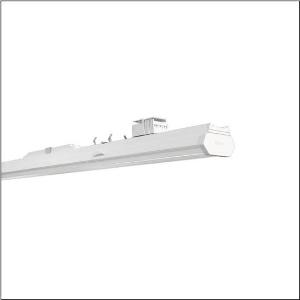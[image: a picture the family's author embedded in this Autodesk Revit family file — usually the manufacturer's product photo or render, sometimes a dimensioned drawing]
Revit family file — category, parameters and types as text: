
# Revit family: licross_r__11_protected_ho_51td11cn4exs_ee6c
name_source: partatom
category: Lighting Fixtures
units: mm (PartAtom-declared; Revit-internal decimal feet)

## family parameters
Cut with Voids When Loaded = No
Host = Face
Light Source = No
Part Type = Normal
Room Calculation Point = No
Round Connector Dimension = Use Diameter
Shared = No

## types (1)
- --- (1 x LED, 14460 lm, 77.6 W, 4000K)
    Apparent Load = 78 VA
    CIE Flux Codes = 84 94 98 99 100
    Color Rendering = 80
    Color Temperature = 4000K
    Default Elevation = 1800 mm
    Description = Licross® 11 Protected HO, luminaire insert, of sheet steel, galvanised, coil coated, white, length: 1.500mm, width: 90mm, height: 101mm, LED rated luminous flux: 14.460lm, light colour: 840, control gear: ON/OFF Multilumen, CLOi, with plug, 3-pole, with phase selection, mains connection: 220..240V, AC, 50/60Hz, start of lifetime: 78W, end of service life: 87W, halogen-free wiring, primary light control with lens, of plastic, primary optical cover: cover, of PMMA, light emission: direct distribution, primary light characteristic: symmetric, protection rating (complete): IP54, insulation class (complete): insulation class I (protective earthing), certification: CE, ENEC, VDE, UKCA, protection symbol: D if used in an environment with non-conductive dust loads with corresponding accessories, impact resistance: IK06, permissible ambient temperature for indoor applications: -35..+35°C, corresponds to IFS (International Featured Standards) requirements for safety and quality in the food industry, reducing of maximum allowable ambient temperature of 5°C with ceiling mounting, LABS conformity tested according to VDMA 24364:2018-05, packaging unit: 1 piece
    Height = 92 mm
    Lamp = 1 x LED
    Lamp Light Flux = 14460 lm
    Lamp Power = 77.6 W
    Lamp count = 1
    Length = 1500 mm
    Luminous efficacy = 186 lm/W
    Manufacturer = Siteco
    ModVariant = No
    Model = 51TD11CN4EXS
    Mounting Place = Ceiling
    Mounting Type = Pendant
    Number of Poles = 1
    OnlyDefault = Yes
    Power Factor = 1
    Product Name = Licross® 11 Protected HO
    Product group = luminaire insert
    ProductGroupID = 901
    Protection Class = Protection class I
    Protection Degree = IP 54
    RLX_Detail_Level = 1
    RLX_Emergency_Light_Flux = 0 lm
    RLX_Emergency_Type = 0
    RLX_Emergency_Type_DB = No
    RlxData = <blob elided: 22125 chars, md5=2f1147d2>
    Socket = socket
    Standby Power = 0 W
    System Light Flux = 14460 lm
    System Power = 78 W
    Type Comments = factory setting: luminous flux: 100 % | (A | C | E) | 181 mA
    Type Image = l_1256145.jpg
    URL = http://relux.com
    VarID = @adj_038025
    Voltage = 0 V
    Weight = 0.00 kg
    Width = 88 mm

## geometry (parser evidence)
native form markers: Blend x4, Sweep x11
no freeform markers — native parametric forms only
